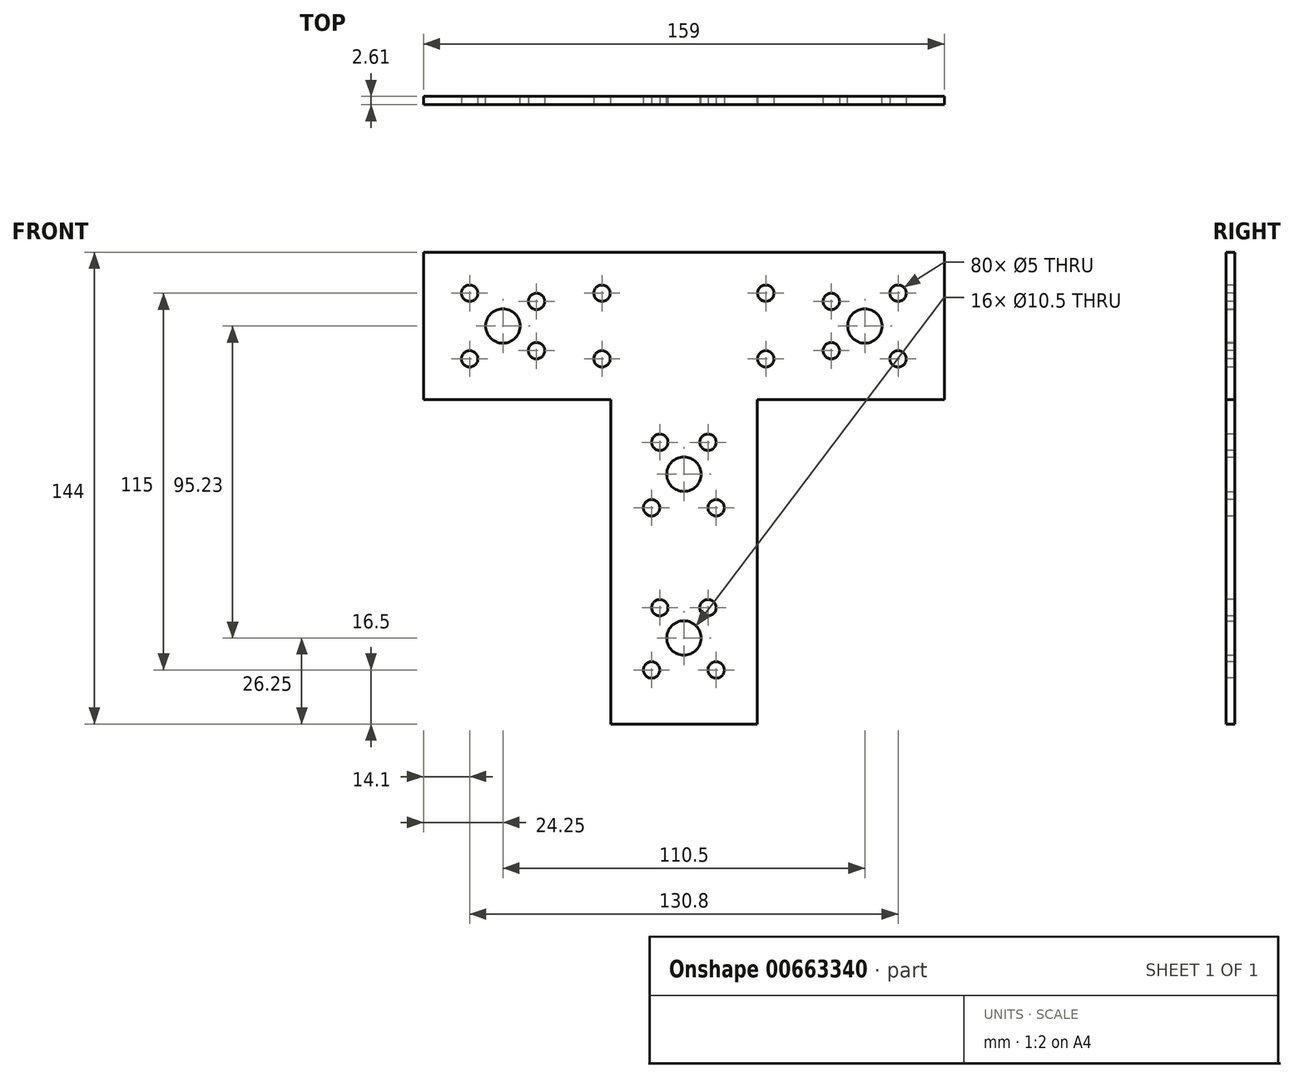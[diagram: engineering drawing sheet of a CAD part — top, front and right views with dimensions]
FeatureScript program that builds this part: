
annotation { "Feature Type Name" : "Feature", "Feature Type Description" : "" }
export const myFeature = defineFeature(function(context is Context, id is Id, definition is map)
    precondition{}
    {
        {
            var Q0;
            Q0=qCreatedBy(makeId("Front.planeOp"),FACE);
            var sketch = newSketch(context, id + "F0", { "sketchPlane" : qUnion([Q0])});
            skLineSegment(sketch, "E0.bottom", {"start": v(79.5, 22.52) * mm, "end": v(-79.5, 22.52) * mm});
            skLineSegment(sketch, "E0.top", {"start": v(79.5, -22.52) * mm, "end": v(22.35, -22.52) * mm});
            skLineSegment(sketch, "E0.left", {"start": v(79.5, 22.52) * mm, "end": v(79.5, -22.52) * mm});
            skLineSegment(sketch, "E0.right", {"start": v(-79.5, 22.52) * mm, "end": v(-79.5, -22.52) * mm});
            skPoint(sketch, "E0.middle", {"position": v(0, 0) * mm});
            skLineSegment(sketch, "E1.top", {"start": v(22.35, -121.48) * mm, "end": v(-22.35, -121.48) * mm});
            skLineSegment(sketch, "E1.left", {"start": v(22.35, -22.52) * mm, "end": v(22.35, -121.48) * mm});
            skLineSegment(sketch, "E1.right", {"start": v(-22.35, -22.52) * mm, "end": v(-22.35, -121.48) * mm});
            skPoint(sketch, "E1.middle", {"position": v(0, -72) * mm});
            skLineSegment(sketch, "E2.trimOffspring", {"start": v(-22.35, -22.52) * mm, "end": v(-79.5, -22.52) * mm});
            skCircle(sketch, "E3", {"center": v(55.25, 0) * mm, "radius": 5.25 * mm});
            skCircle(sketch, "E4", {"center": v(-55.25, 0) * mm, "radius": 5.25 * mm});
            skLineSegment(sketch, "E5", {"start": v(0, -39.98) * mm, "end": v(0, -50.48) * mm});
            skCircle(sketch, "E6", {"center": v(0, -95.23) * mm, "radius": 5.25 * mm});
            skCircle(sketch, "E7", {"center": v(0, -45.23) * mm, "radius": 5.25 * mm});
            skLineSegment(sketch, "E8.trimOffspring", {"start": v(55.25, 5.25) * mm, "end": v(55.25, -5.25) * mm});
            skPoint(sketch, "E9.start.orphan", {"position": v(55.25, 40.87) * mm});
            skPoint(sketch, "E10.trimOffspring.end.orphan", {"position": v(55.25, -30.6) * mm});
            skLineSegment(sketch, "E11.trimOffspring", {"start": v(-55.25, 5.25) * mm, "end": v(-55.25, -5.25) * mm});
            skPoint(sketch, "E12.start.orphan", {"position": v(-55.25, 40.87) * mm});
            skPoint(sketch, "E13.trimOffspring.end.orphan", {"position": v(-55.25, -30.6) * mm});
            skLineSegment(sketch, "E14.trimOffspring", {"start": v(-5.25, -45.23) * mm, "end": v(5.25, -45.23) * mm});
            skPoint(sketch, "E15.start.orphan", {"position": v(-33.39, -48.7) * mm});
            skLineSegment(sketch, "E16.trimOffspring", {"start": v(-5.25, -95.23) * mm, "end": v(5.25, -95.23) * mm});
            skPoint(sketch, "E17.trimOffspring.end.orphan", {"position": v(-33.39, -99.2) * mm});
            skLineSegment(sketch, "E18.trimOffspring", {"start": v(5.25, -95.23) * mm, "end": v(-5.25, -95.23) * mm});
            skLineSegment(sketch, "E19.trimOffspring", {"start": v(0, -89.98) * mm, "end": v(0, -100.48) * mm});
            skPoint(sketch, "E20.orphan", {"position": v(0, 74.47) * mm});
            skSolve(sketch);
        }
        {
            var Q0;
            Q0=makeQuery(id+"F0.imprint","IMPRINT",FACE,{"disambiguationData":[TD([[makeQuery(id+"F0.imprint","IMPRINT",EDGE,{"derivedFrom":sQuery(id+"F0.wireOp",EDGE,"E0.bottom")}),1.0]])]});
            extrude(context, id + "F1", {"entities" : qUnion([Q0]), "depth" : 2.6 * mm, "offsetDistance" : 25 * mm});
        }
        {
            var Q0;
            Q0=makeQuery(id+"F1.opExtrude","CAP_FACE",FACE,{"disambiguationData":[OSD([sQuery(id+"F0.wireOp",EDGE,"E0.bottom"),sQuery(id+"F0.wireOp",EDGE,"E0.top"),sQuery(id+"F0.wireOp",EDGE,"E0.left"),sQuery(id+"F0.wireOp",EDGE,"E0.right"),sQuery(id+"F0.wireOp",EDGE,"E1.top"),sQuery(id+"F0.wireOp",EDGE,"E1.left"),sQuery(id+"F0.wireOp",EDGE,"E1.right"),sQuery(id+"F0.wireOp",EDGE,"E2.trimOffspring"),sQuery(id+"F0.wireOp",EDGE,"E3"),sQuery(id+"F0.wireOp",EDGE,"E4"),sQuery(id+"F0.wireOp",EDGE,"E6"),sQuery(id+"F0.wireOp",EDGE,"E7")])],"isStart":false});
            var sketch = newSketch(context, id + "F2", { "sketchPlane" : qUnion([Q0])});
            skLineSegment(sketch, "E21", {"start": v(65.4, 33.53) * mm, "end": v(65.4, 0) * mm, "construction": true});
            skLineSegment(sketch, "E22", {"start": v(90.2, 10.02) * mm, "end": v(44.43, 10.02) * mm, "construction": true});
            skCircle(sketch, "E23", {"center": v(65.4, 10.02) * mm, "radius": 2.5 * mm});
            skLineSegment(sketch, "E24", {"start": v(65.4, 0) * mm, "end": v(65.4, -22.52) * mm, "construction": true});
            skLineSegment(sketch, "E25", {"start": v(90.2, -10.02) * mm, "end": v(53.36, -10.02) * mm, "construction": true});
            skCircle(sketch, "E26", {"center": v(65.4, -10.02) * mm, "radius": 2.5 * mm});
            skLineSegment(sketch, "E27", {"start": v(50.9, 7.52) * mm, "end": v(35.66, 7.52) * mm, "construction": true});
            skLineSegment(sketch, "E28", {"start": v(45, 15.07) * mm, "end": v(45, 2.9) * mm, "construction": true});
            skCircle(sketch, "E29", {"center": v(45, 7.52) * mm, "radius": 2.5 * mm});
            skLineSegment(sketch, "E30", {"start": v(38.69, -7.52) * mm, "end": v(54.75, -7.52) * mm, "construction": true});
            skLineSegment(sketch, "E31", {"start": v(45, -18.4) * mm, "end": v(45, 2.9) * mm, "construction": true});
            skCircle(sketch, "E32", {"center": v(45, -7.52) * mm, "radius": 2.5 * mm});
            skPoint(sketch, "E32.centerSnap0", {"position": v(45, -7.75) * mm});
            skLineSegment(sketch, "E33", {"start": v(25, 29.53) * mm, "end": v(25, -34.38) * mm, "construction": true});
            skLineSegment(sketch, "E34", {"start": v(50.56, 10.02) * mm, "end": v(12.08, 10.02) * mm, "construction": true});
            skLineSegment(sketch, "E35", {"start": v(55.96, -10.02) * mm, "end": v(18.44, -10.02) * mm, "construction": true});
            skCircle(sketch, "E36", {"center": v(25, 10.02) * mm, "radius": 2.5 * mm});
            skCircle(sketch, "E37", {"center": v(25, -10.02) * mm, "radius": 2.5 * mm});
            skLineSegment(sketch, "E38", {"start": v(15.09, 10.02) * mm, "end": v(-79.5, 10.02) * mm, "construction": true});
            skLineSegment(sketch, "E39", {"start": v(21.13, -10.02) * mm, "end": v(-81.1, -10.02) * mm, "construction": true});
            skLineSegment(sketch, "E40", {"start": v(40.69, -7.52) * mm, "end": v(-72.68, -7.52) * mm, "construction": true});
            skLineSegment(sketch, "E41", {"start": v(37.82, 7.52) * mm, "end": v(-72.52, 7.52) * mm, "construction": true});
            skLineSegment(sketch, "E42", {"start": v(-25, 44.36) * mm, "end": v(-25, -30.05) * mm, "construction": true});
            skCircle(sketch, "E43", {"center": v(-25, 10.02) * mm, "radius": 2.5 * mm});
            skCircle(sketch, "E44", {"center": v(-25, -10.02) * mm, "radius": 2.5 * mm});
            skLineSegment(sketch, "E45", {"start": v(-45, 27.11) * mm, "end": v(-45, -17.28) * mm, "construction": true});
            skCircle(sketch, "E46", {"center": v(-45, 7.52) * mm, "radius": 2.5 * mm});
            skCircle(sketch, "E47", {"center": v(-45, -7.52) * mm, "radius": 2.5 * mm});
            skLineSegment(sketch, "E48", {"start": v(-65.4, 17.62) * mm, "end": v(-65.4, -11.96) * mm, "construction": true});
            skCircle(sketch, "E49", {"center": v(-65.4, -10.02) * mm, "radius": 2.5 * mm});
            skCircle(sketch, "E50", {"center": v(-65.4, 10.02) * mm, "radius": 2.5 * mm});
            skLineSegment(sketch, "E51", {"start": v(9.85, -31.34) * mm, "end": v(9.85, -115.67) * mm, "construction": true});
            skLineSegment(sketch, "E52", {"start": v(-9.85, -31.34) * mm, "end": v(-9.85, -114.16) * mm, "construction": true});
            skLineSegment(sketch, "E53", {"start": v(-22.35, -104.98) * mm, "end": v(33.55, -104.98) * mm, "construction": true});
            skLineSegment(sketch, "E54", {"start": v(29.4, -55.48) * mm, "end": v(-30.77, -55.48) * mm, "construction": true});
            skCircle(sketch, "E55", {"center": v(9.85, -55.48) * mm, "radius": 2.5 * mm});
            skCircle(sketch, "E56", {"center": v(-9.85, -55.48) * mm, "radius": 2.5 * mm});
            skLineSegment(sketch, "E57", {"start": v(-14.52, -35.48) * mm, "end": v(16.5, -35.48) * mm, "construction": true});
            skCircle(sketch, "E58", {"center": v(-9.85, -104.98) * mm, "radius": 2.5 * mm});
            skCircle(sketch, "E59", {"center": v(9.85, -104.98) * mm, "radius": 2.5 * mm});
            skLineSegment(sketch, "E60", {"start": v(-7.35, -31.34) * mm, "end": v(-7.35, -52.3) * mm, "construction": true});
            skLineSegment(sketch, "E61", {"start": v(7.35, -31.34) * mm, "end": v(7.35, -49.7) * mm, "construction": true});
            skCircle(sketch, "E62", {"center": v(-7.35, -35.48) * mm, "radius": 2.5 * mm});
            skCircle(sketch, "E63", {"center": v(7.35, -35.48) * mm, "radius": 2.5 * mm});
            skLineSegment(sketch, "E64", {"start": v(-7.35, -52.3) * mm, "end": v(-7.35, -98.5) * mm, "construction": true});
            skLineSegment(sketch, "E65", {"start": v(7.35, -49.7) * mm, "end": v(7.35, -98.5) * mm, "construction": true});
            skLineSegment(sketch, "E66", {"start": v(-21.14, -85.98) * mm, "end": v(20.05, -85.98) * mm, "construction": true});
            skCircle(sketch, "E67", {"center": v(7.35, -85.98) * mm, "radius": 2.5 * mm});
            skCircle(sketch, "E68", {"center": v(-7.35, -85.98) * mm, "radius": 2.5 * mm});
            skSolve(sketch);
        }
        {
            var Q0;
            Q0 = qSketchRegion(id + "F2", true);
            extrude(context, id + "F3", {"entities" : qUnion([Q0]), "operationType" : NewBodyOperationType.REMOVE, "endBound" : BoundingType.THROUGH_ALL, "oppositeDirection" : true, "depth" : 25 * mm, "offsetDistance" : 25 * mm});
        }
    });
